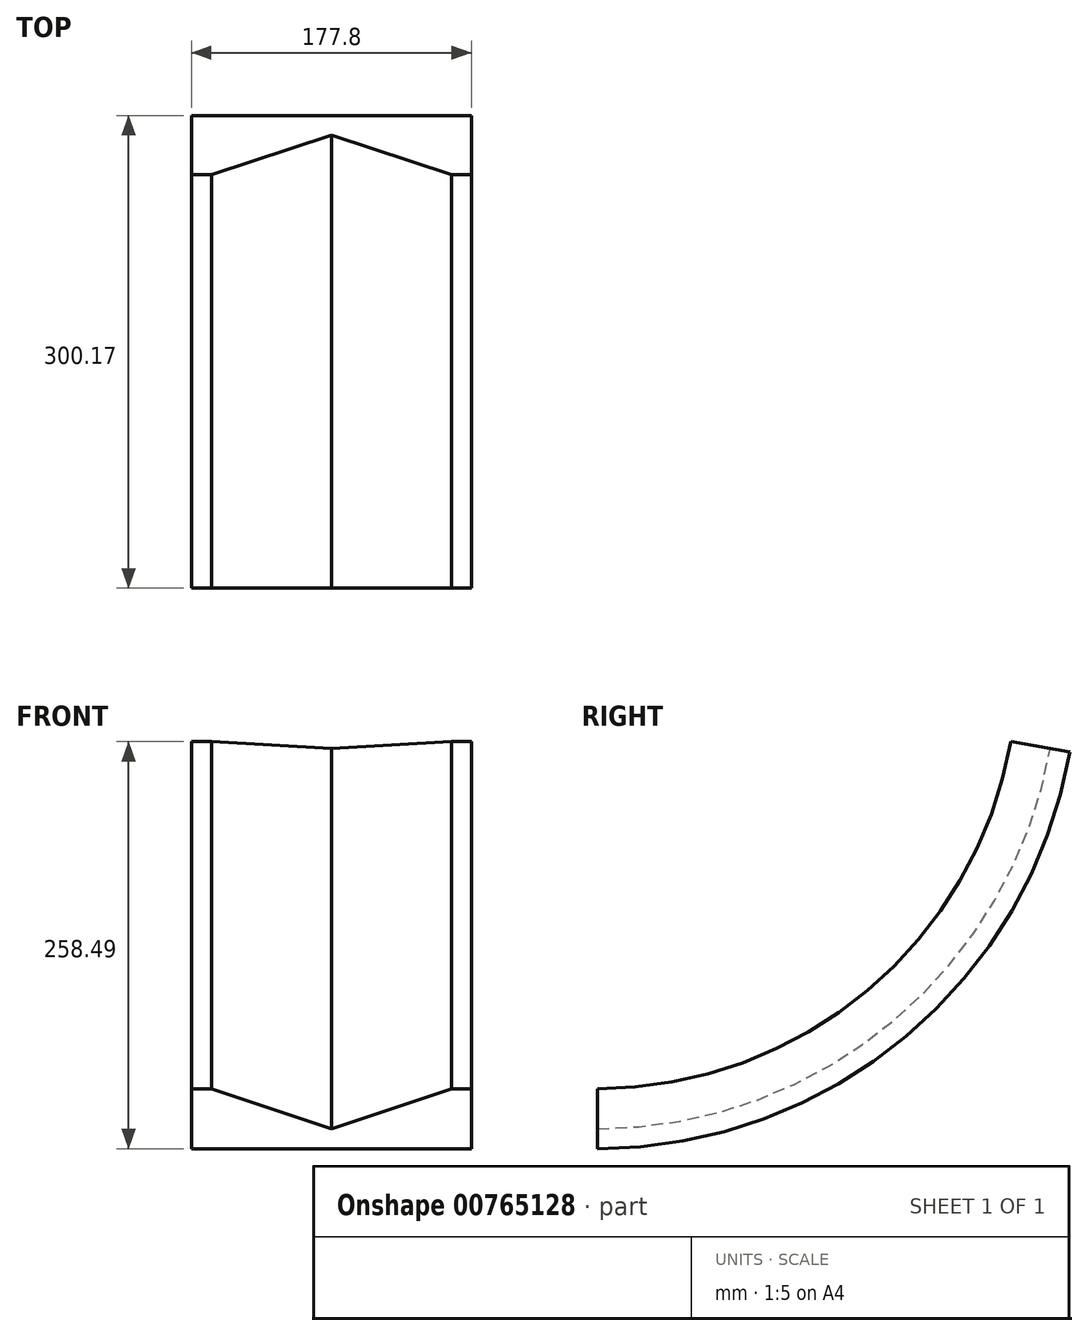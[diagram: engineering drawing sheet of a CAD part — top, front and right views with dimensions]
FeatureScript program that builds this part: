
annotation { "Feature Type Name" : "Feature", "Feature Type Description" : "" }
export const myFeature = defineFeature(function(context is Context, id is Id, definition is map)
    precondition{}
    {
        {
            var Q0;
            Q0=qCreatedBy(makeId("Front.planeOp"),FACE);
            var sketch = newSketch(context, id + "F0", { "sketchPlane" : qUnion([Q0])});
            skLineSegment(sketch, "E0", {"start": v(0, 0) * mm, "end": v(177.8, 0) * mm});
            skLineSegment(sketch, "E1", {"start": v(177.8, 0) * mm, "end": v(177.8, 38.1) * mm});
            skLineSegment(sketch, "E2", {"start": v(177.8, 38.1) * mm, "end": v(165.1, 38.1) * mm});
            skLineSegment(sketch, "E3", {"start": v(88.9, 12.7) * mm, "end": v(88.9, 12.7) * mm});
            skLineSegment(sketch, "E4", {"start": v(12.7, 38.1) * mm, "end": v(0, 38.1) * mm});
            skLineSegment(sketch, "E5", {"start": v(0, 38.1) * mm, "end": v(0, 0) * mm});
            skLineSegment(sketch, "E6", {"start": v(12.7, 38.1) * mm, "end": v(88.9, 12.7) * mm});
            skLineSegment(sketch, "E7", {"start": v(165.1, 38.1) * mm, "end": v(88.9, 12.7) * mm});
            skSolve(sketch);
        }
        {
            var Q0;
            Q0=qCreatedBy(makeId("Front.planeOp"),FACE);
            var sketch = newSketch(context, id + "F1", { "sketchPlane" : qUnion([Q0])});
            skLineSegment(sketch, "E8", {"start": v(0, 304.8) * mm, "end": v(232.83, 304.8) * mm, "construction": true});
            skSolve(sketch);
        }
        {
            var Q0;
            Q0=qSketchRegion(id+"F0",true);
            var Q1;
            Q1=sQuery(id+"F1.wireOp",EDGE,"E8");
            revolve(context, id + "F2", {"entities" : qUnion([Q0]), "axis" : qUnion([Q1]), "revolveType" : RevolveType.ONE_DIRECTION, "angle" : 80 * degree});
        }
    });
